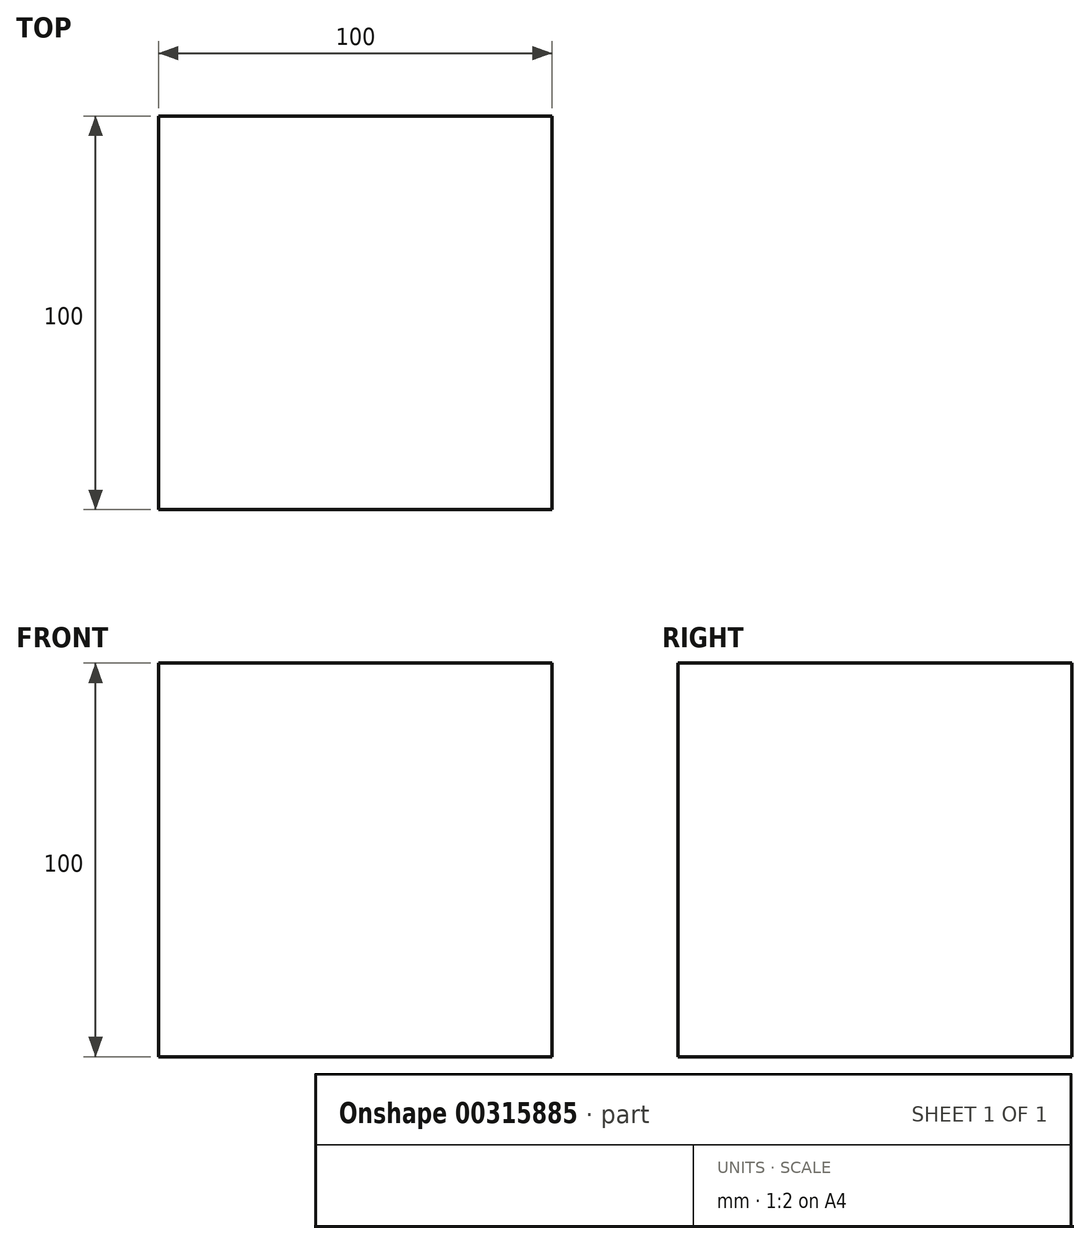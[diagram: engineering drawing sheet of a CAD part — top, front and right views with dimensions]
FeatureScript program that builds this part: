
annotation { "Feature Type Name" : "Feature", "Feature Type Description" : "" }
export const myFeature = defineFeature(function(context is Context, id is Id, definition is map)
    precondition{}
    {
        {
            var Q0;
            Q0=qCreatedBy(makeId("Front.planeOp"),FACE);
            var sketch = newSketch(context, id + "F0", { "sketchPlane" : qUnion([Q0])});
            skLineSegment(sketch, "E0.bottom", {"start": v(0, 0) * mm, "end": v(100, 0) * mm});
            skLineSegment(sketch, "E0.top", {"start": v(0, 100) * mm, "end": v(100, 100) * mm});
            skLineSegment(sketch, "E0.left", {"start": v(0, 0) * mm, "end": v(0, 100) * mm});
            skLineSegment(sketch, "E0.right", {"start": v(100, 0) * mm, "end": v(100, 100) * mm});
            skSolve(sketch);
        }
        {
            var Q0;
            Q0 = qSketchRegion(id + "F0", true);
            extrude(context, id + "F1", {"entities" : qUnion([Q0]), "depth" : 100 * mm});
        }
    });
